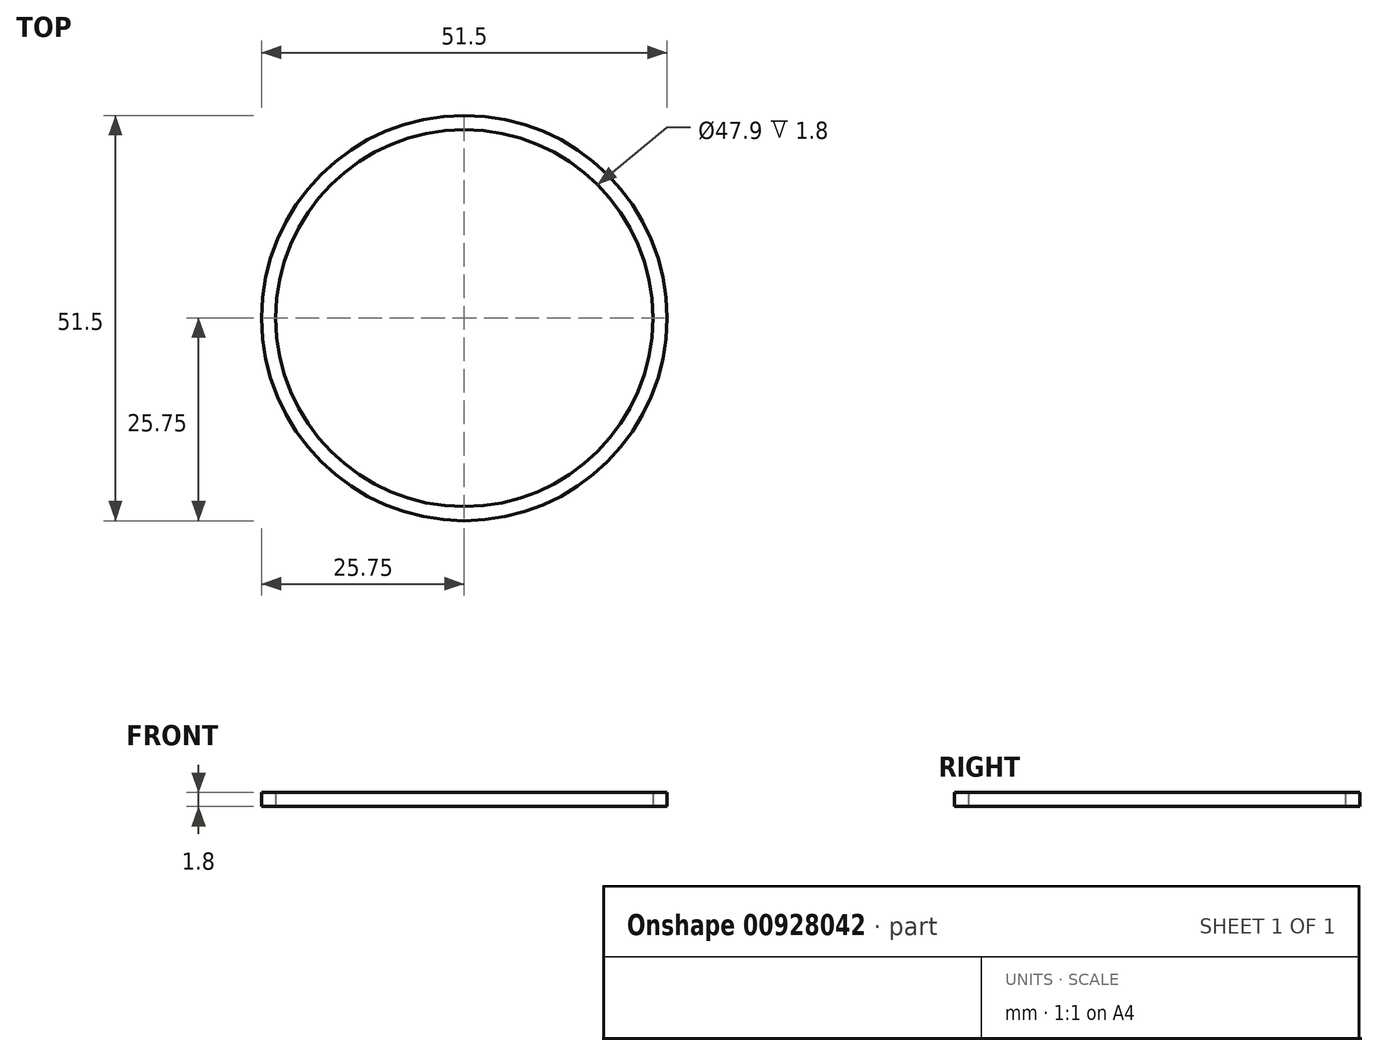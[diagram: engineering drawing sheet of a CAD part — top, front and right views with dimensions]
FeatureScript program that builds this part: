
annotation { "Feature Type Name" : "Feature", "Feature Type Description" : "" }
export const myFeature = defineFeature(function(context is Context, id is Id, definition is map)
    precondition{}
    {
        {
            var Q0;
            Q0=qCreatedBy(makeId("Front.planeOp"),FACE);
            var sketch = newSketch(context, id + "F0", { "sketchPlane" : qUnion([Q0])});
            skLineSegment(sketch, "E0", {"start": v(0, -46.5) * mm, "end": v(0, 61.6) * mm, "construction": true});
            skLineSegment(sketch, "E1.bottom", {"start": v(25.75, -0.9) * mm, "end": v(23.95, -0.9) * mm});
            skLineSegment(sketch, "E1.top", {"start": v(25.75, 0.9) * mm, "end": v(23.95, 0.9) * mm});
            skLineSegment(sketch, "E1.left", {"start": v(25.75, -0.9) * mm, "end": v(25.75, 0.9) * mm});
            skLineSegment(sketch, "E1.right", {"start": v(23.95, -0.9) * mm, "end": v(23.95, 0.9) * mm});
            skPoint(sketch, "E1.middle", {"position": v(24.85, 0) * mm});
            skSolve(sketch);
        }
        {
            var Q0;
            Q0=makeQuery(id+"F0.imprint","IMPRINT",FACE,{"disambiguationData":[TD([[makeQuery(id+"F0.imprint","IMPRINT",EDGE,{"derivedFrom":sQuery(id+"F0.wireOp",EDGE,"E1.bottom")}),-1.0]])]});
            var Q1;
            Q1=sQuery(id+"F0.wireOp",EDGE,"SwxsdONq-bUCt-Qqg1-PfAN-7CW4sGTHIzxG");
            var Q2;
            Q2=sQuery(id+"F0.wireOp",EDGE,"E0");
            revolve(context, id + "F1", {"surfaceOperationType" : NewSurfaceOperationType.NEW, "entities" : qUnion([Q0]), "surfaceEntities" : qUnion([Q1]), "axis" : qUnion([Q2]), "revolveType" : RevolveType.FULL});
        }
    });
